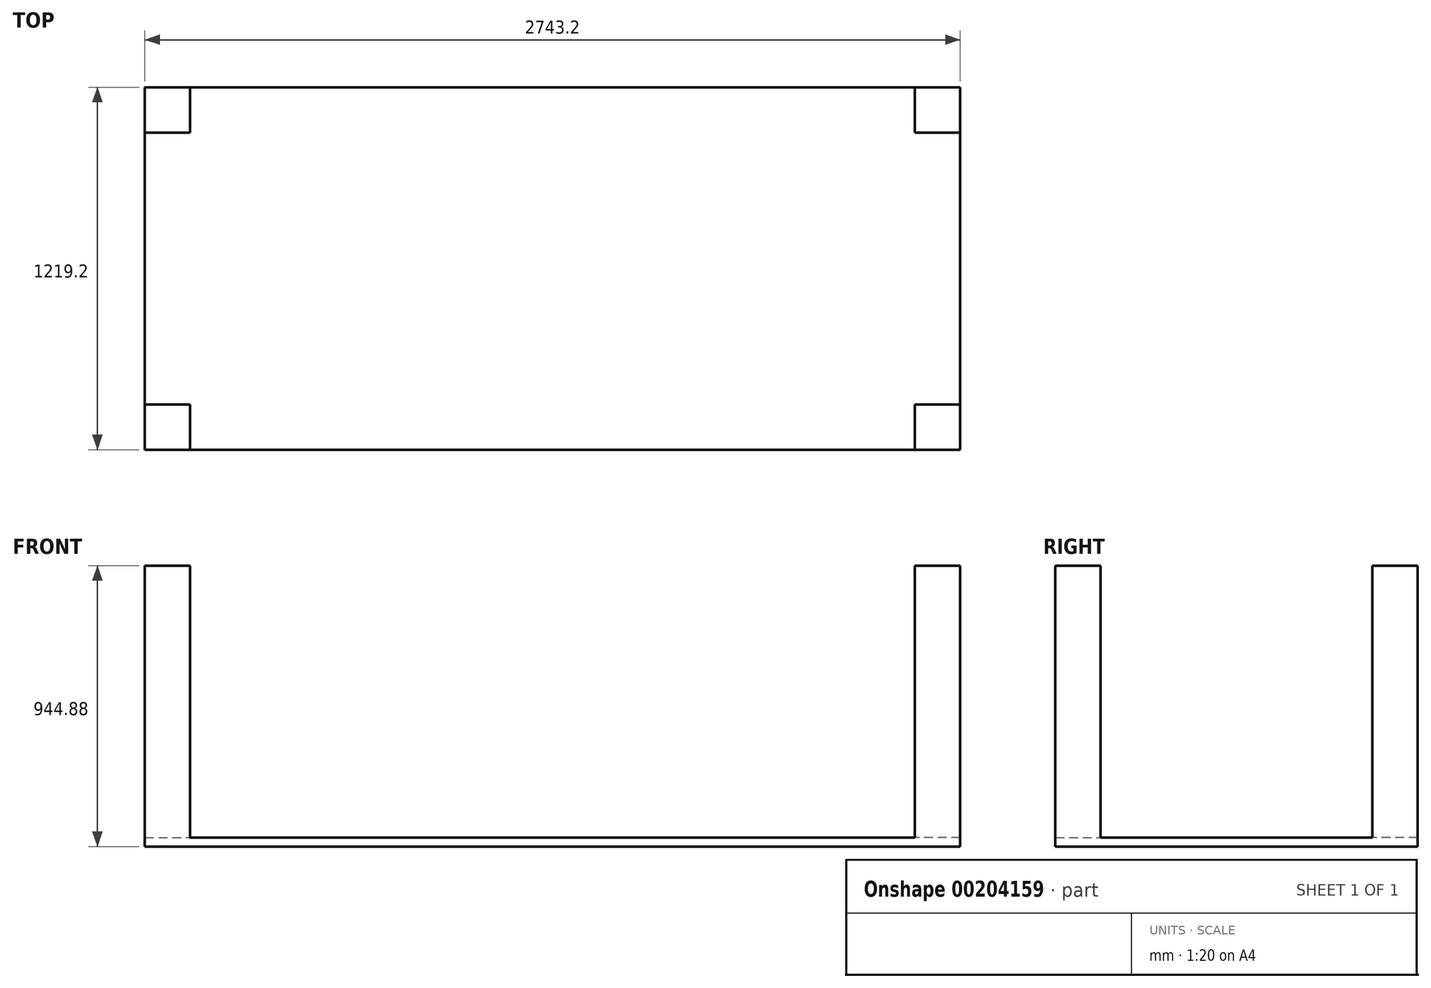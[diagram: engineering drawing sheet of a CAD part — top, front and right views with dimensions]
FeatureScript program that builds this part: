
annotation { "Feature Type Name" : "Feature", "Feature Type Description" : "" }
export const myFeature = defineFeature(function(context is Context, id is Id, definition is map)
    precondition{}
    {
        {
            var Q0;
            Q0=qCreatedBy(makeId("Top.planeOp"),FACE);
            var sketch = newSketch(context, id + "F0", { "sketchPlane" : qUnion([Q0])});
            skLineSegment(sketch, "E0.bottom", {"start": v(0, 0) * mm, "end": v(2743.2, 0) * mm});
            skLineSegment(sketch, "E0.top", {"start": v(0, 1219.2) * mm, "end": v(2743.2, 1219.2) * mm});
            skLineSegment(sketch, "E0.left", {"start": v(0, 0) * mm, "end": v(0, 1219.2) * mm});
            skLineSegment(sketch, "E0.right", {"start": v(2743.2, 0) * mm, "end": v(2743.2, 1219.2) * mm});
            skSolve(sketch);
        }
        {
            var Q0;
            Q0=makeQuery(id+"F0.imprint","IMPRINT",FACE,{"disambiguationData":[TD([[makeQuery(id+"F0.imprint","IMPRINT",EDGE,{"derivedFrom":sQuery(id+"F0.wireOp",EDGE,"E0.bottom")}),1.0]])]});
            extrude(context, id + "F1", {"entities" : qUnion([Q0]), "depth" : 30.48 * mm});
        }
        {
            var Q0;
            Q0=makeQuery(id+"F1.opExtrude","CAP_FACE",FACE,{"disambiguationData":[OSD([sQuery(id+"F0.wireOp",EDGE,"E0.bottom"),sQuery(id+"F0.wireOp",EDGE,"E0.top"),sQuery(id+"F0.wireOp",EDGE,"E0.left"),sQuery(id+"F0.wireOp",EDGE,"E0.right")])],"isStart":false});
            var sketch = newSketch(context, id + "F2", { "sketchPlane" : qUnion([Q0])});
            skLineSegment(sketch, "E1.bottom", {"start": v(0, 1219.2) * mm, "end": v(152.4, 1219.2) * mm});
            skLineSegment(sketch, "E1.top", {"start": v(0, 1066.8) * mm, "end": v(152.4, 1066.8) * mm});
            skLineSegment(sketch, "E1.left", {"start": v(0, 1219.2) * mm, "end": v(0, 1066.8) * mm});
            skLineSegment(sketch, "E1.right", {"start": v(152.4, 1219.2) * mm, "end": v(152.4, 1066.8) * mm});
            skLineSegment(sketch, "E2.bottom", {"start": v(0, 0) * mm, "end": v(152.4, 0) * mm});
            skLineSegment(sketch, "E2.top", {"start": v(0, 152.4) * mm, "end": v(152.4, 152.4) * mm});
            skLineSegment(sketch, "E2.left", {"start": v(0, 0) * mm, "end": v(0, 152.4) * mm});
            skLineSegment(sketch, "E2.right", {"start": v(152.4, 0) * mm, "end": v(152.4, 152.4) * mm});
            skLineSegment(sketch, "E3.bottom", {"start": v(2743.2, 1219.2) * mm, "end": v(2590.8, 1219.2) * mm});
            skLineSegment(sketch, "E3.top", {"start": v(2743.2, 1066.8) * mm, "end": v(2590.8, 1066.8) * mm});
            skLineSegment(sketch, "E3.left", {"start": v(2743.2, 1219.2) * mm, "end": v(2743.2, 1066.8) * mm});
            skLineSegment(sketch, "E3.right", {"start": v(2590.8, 1219.2) * mm, "end": v(2590.8, 1066.8) * mm});
            skLineSegment(sketch, "E4.bottom", {"start": v(2743.2, 0) * mm, "end": v(2590.8, 0) * mm});
            skLineSegment(sketch, "E4.top", {"start": v(2743.2, 152.4) * mm, "end": v(2590.8, 152.4) * mm});
            skLineSegment(sketch, "E4.left", {"start": v(2743.2, 0) * mm, "end": v(2743.2, 152.4) * mm});
            skLineSegment(sketch, "E4.right", {"start": v(2590.8, 0) * mm, "end": v(2590.8, 152.4) * mm});
            skSolve(sketch);
        }
        {
            var Q0;
            Q0=makeQuery(id+"F2.imprint","IMPRINT",FACE,{"disambiguationData":[TD([[makeQuery(id+"F2.imprint","IMPRINT",EDGE,{"derivedFrom":sQuery(id+"F2.wireOp",EDGE,"E2.bottom")}),1.0]])]});
            var Q1;
            Q1=makeQuery(id+"F2.imprint","IMPRINT",FACE,{"disambiguationData":[TD([[makeQuery(id+"F2.imprint","IMPRINT",EDGE,{"derivedFrom":sQuery(id+"F2.wireOp",EDGE,"E3.bottom")}),-1.0]])]});
            var Q2;
            Q2=makeQuery(id+"F2.imprint","IMPRINT",FACE,{"disambiguationData":[TD([[makeQuery(id+"F2.imprint","IMPRINT",EDGE,{"derivedFrom":sQuery(id+"F2.wireOp",EDGE,"E4.bottom")}),1.0]])]});
            var Q3;
            Q3=makeQuery(id+"F2.imprint","IMPRINT",FACE,{"disambiguationData":[TD([[makeQuery(id+"F2.imprint","IMPRINT",EDGE,{"derivedFrom":sQuery(id+"F2.wireOp",EDGE,"E1.bottom")}),-1.0]])]});
            extrude(context, id + "F3", {"entities" : qUnion([Q0, Q1, Q2, Q3]), "operationType" : NewBodyOperationType.ADD, "depth" : 914.4 * mm});
        }
    });
